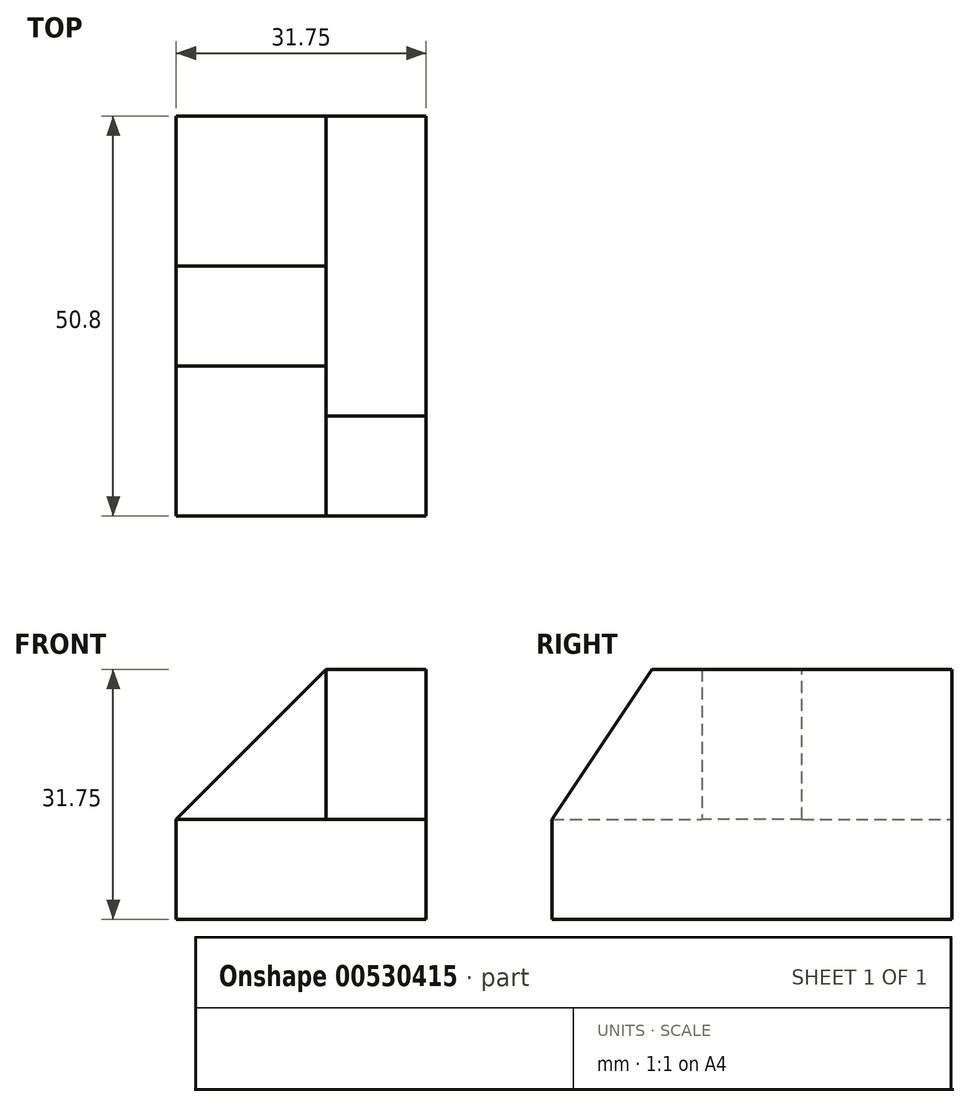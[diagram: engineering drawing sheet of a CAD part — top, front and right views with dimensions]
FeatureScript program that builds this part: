
annotation { "Feature Type Name" : "Feature", "Feature Type Description" : "" }
export const myFeature = defineFeature(function(context is Context, id is Id, definition is map)
    precondition{}
    {
        {
            var Q0;
            Q0=qCreatedBy(makeId("Front.planeOp"),FACE);
            var sketch = newSketch(context, id + "F0", { "sketchPlane" : qUnion([Q0])});
            skLineSegment(sketch, "E0", {"start": v(-34.15, 0) * mm, "end": v(-2.4, 0) * mm});
            skLineSegment(sketch, "E1", {"start": v(-2.4, 0) * mm, "end": v(-2.4, 31.75) * mm});
            skLineSegment(sketch, "E2", {"start": v(-2.4, 31.75) * mm, "end": v(-15.1, 31.75) * mm});
            skLineSegment(sketch, "E3", {"start": v(-15.1, 31.75) * mm, "end": v(-15.1, 12.7) * mm});
            skLineSegment(sketch, "E4", {"start": v(-15.1, 12.7) * mm, "end": v(-34.44, 12.7) * mm});
            skLineSegment(sketch, "E5", {"start": v(-34.15, 13.03) * mm, "end": v(-34.15, 0) * mm});
            skSolve(sketch);
        }
        {
            var Q0;
            {var subQ1=sQuery(id+"F0.wireOp",EDGE,"E0");Q0=makeQuery(id+"F0.imprint","IMPRINT",FACE,{"disambiguationData":[TD([[makeQuery(id+"F0.imprint","IMPRINT",EDGE,{"derivedFrom":subQ1}),1.0]])]});}
            extrude(context, id + "F1", {"entities" : qUnion([Q0]), "depth" : 50.8 * mm, "offsetDistance" : 25.4 * mm});
        }
        {
            var Q0;
            Q0=makeQuery(id+"F1.opExtrude","SWEPT_FACE",FACE,{"disambiguationData":[OSD([sQuery(id+"F0.wireOp",EDGE,"E3")])]});
            var sketch = newSketch(context, id + "F2", { "sketchPlane" : qUnion([Q0])});
            skLineSegment(sketch, "E6", {"start": v(38.1, 31.75) * mm, "end": v(50.8, 12.7) * mm});
            skSolve(sketch);
        }
        {
            var Q0;
            {var subQ0=sQuery(id+"F2.wireOp",EDGE,"E6");Q0=makeQuery(id+"F2.imprint","IMPRINT",FACE,{"disambiguationData":[TD([[makeQuery(id+"F2.imprint","IMPRINT",EDGE,{"derivedFrom":subQ0}),1.0]])]});}
            extrude(context, id + "F3", {"entities" : qUnion([Q0]), "operationType" : NewBodyOperationType.REMOVE, "endBound" : BoundingType.THROUGH_ALL, "oppositeDirection" : true, "depth" : 25.4 * mm, "offsetDistance" : 25.4 * mm});
        }
        {
            var Q0;
            Q0=makeQuery(id+"F1.opExtrude","SWEPT_FACE",FACE,{"disambiguationData":[OSD([sQuery(id+"F0.wireOp",EDGE,"E4")])]});
            var sketch = newSketch(context, id + "F4", { "sketchPlane" : qUnion([Q0])});
            skLineSegment(sketch, "E7", {"start": v(-34.15, -19.05) * mm, "end": v(-15.1, -19.05) * mm});
            skLineSegment(sketch, "E8", {"start": v(-34.15, -31.75) * mm, "end": v(-15.1, -31.75) * mm});
            skSolve(sketch);
        }
        {
            var Q0;
            {var subQ0=sQuery(id+"F4.wireOp",EDGE,"E7");Q0=makeQuery(id+"F4.imprint","IMPRINT",FACE,{"disambiguationData":[TD([[makeQuery(id+"F4.imprint","IMPRINT",EDGE,{"derivedFrom":subQ0}),-1.0]])]});}
            extrude(context, id + "F5", {"entities" : qUnion([Q0]), "operationType" : NewBodyOperationType.ADD, "depth" : 19.05 * mm, "offsetDistance" : 25.4 * mm});
        }
        {
            var Q0;
            Q0=makeQuery(id+"F5.opExtrude","SWEPT_FACE",FACE,{"disambiguationData":[OSD([sQuery(id+"F4.wireOp",EDGE,"E8")])]});
            var sketch = newSketch(context, id + "F6", { "sketchPlane" : qUnion([Q0])});
            skLineSegment(sketch, "E9", {"start": v(-15.1, 31.75) * mm, "end": v(-34.15, 12.7) * mm});
            skSolve(sketch);
        }
        {
            var Q0;
            Q0=makeQuery(id+"F6.imprint","IMPRINT",FACE,{"disambiguationData":[TD([[makeQuery(id+"F6.imprint","IMPRINT",EDGE,{"derivedFrom":sQuery(id+"F6.wireOp",EDGE,"E9")}),-1.0]])]});
            extrude(context, id + "F7", {"entities" : qUnion([Q0]), "operationType" : NewBodyOperationType.REMOVE, "oppositeDirection" : true, "depth" : 25.4 * mm, "offsetDistance" : 25.4 * mm});
        }
    });
